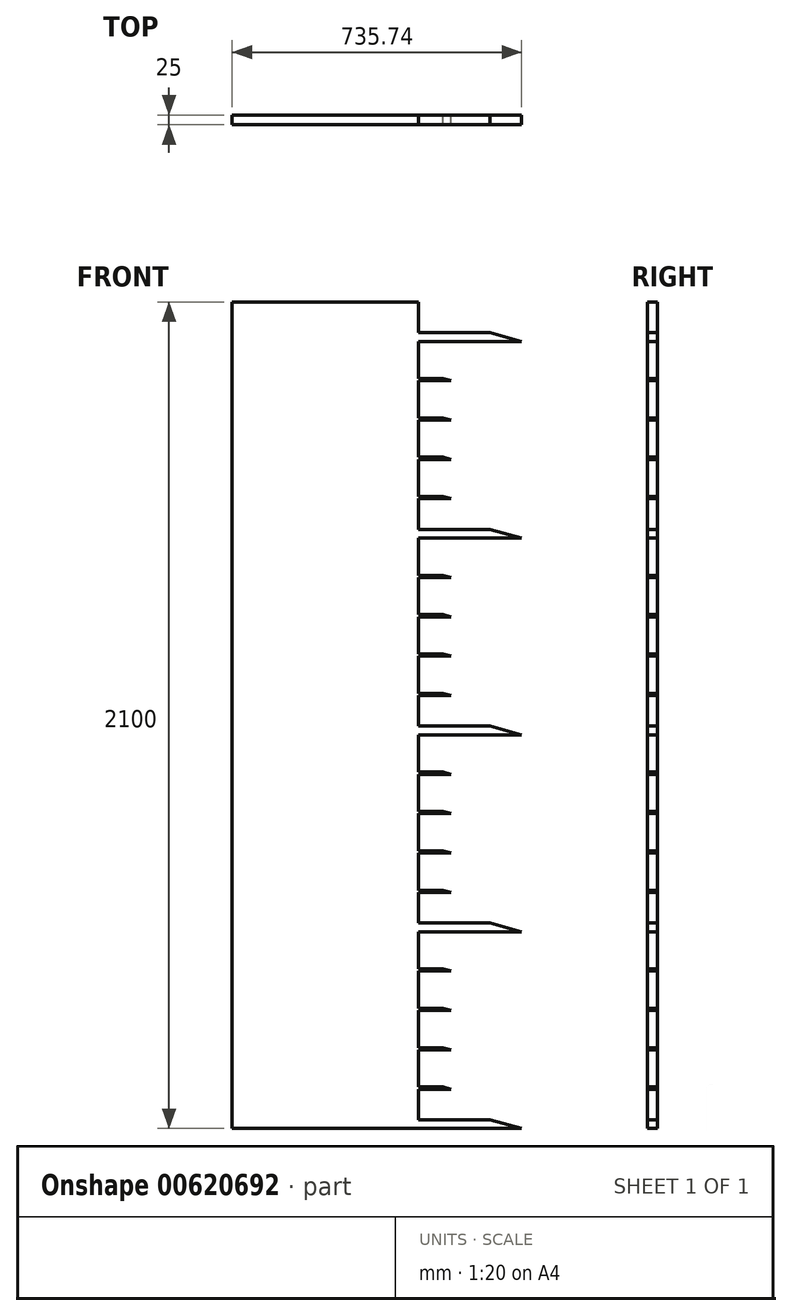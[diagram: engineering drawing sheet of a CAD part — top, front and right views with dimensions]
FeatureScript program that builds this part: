
annotation { "Feature Type Name" : "Feature", "Feature Type Description" : "" }
export const myFeature = defineFeature(function(context is Context, id is Id, definition is map)
    precondition{}
    {
        {
            var Q0;
            Q0=qCreatedBy(makeId("Front.planeOp"),FACE);
            var sketch = newSketch(context, id + "F0", { "sketchPlane" : qUnion([Q0])});
            skLineSegment(sketch, "E0.bottom", {"start": v(0, 0) * mm, "end": v(474.15, 0) * mm});
            skLineSegment(sketch, "E0.top", {"start": v(0, 2100) * mm, "end": v(474.15, 2100) * mm});
            skLineSegment(sketch, "E0.left", {"start": v(0, 0) * mm, "end": v(0, 2100) * mm});
            skLineSegment(sketch, "E0.right", {"start": v(474.15, 0) * mm, "end": v(474.15, 2100) * mm});
            skLineSegment(sketch, "E1.bottom", {"start": v(474.15, 0) * mm, "end": v(735.74, 0) * mm});
            skLineSegment(sketch, "E1.top", {"start": v(474.15, 22.4) * mm, "end": v(655.59, 22.4) * mm});
            skLineSegment(sketch, "E1.left", {"start": v(474.15, 0) * mm, "end": v(474.15, 22.4) * mm});
            skLineSegment(sketch, "E1.right", {"start": v(735.74, 0) * mm, "end": v(655.59, 22.4) * mm});
            skLineSegment(sketch, "E2.0.1.0", {"start": v(735.74, 500) * mm, "end": v(655.59, 522.4) * mm});
            skLineSegment(sketch, "E2.0.1.1", {"start": v(474.15, 500) * mm, "end": v(474.15, 522.4) * mm});
            skLineSegment(sketch, "E2.0.1.2", {"start": v(474.15, 522.4) * mm, "end": v(655.59, 522.4) * mm});
            skLineSegment(sketch, "E2.0.1.3", {"start": v(474.15, 500) * mm, "end": v(735.74, 500) * mm});
            skLineSegment(sketch, "E2.0.2.0", {"start": v(735.74, 1000) * mm, "end": v(655.59, 1022.4) * mm});
            skLineSegment(sketch, "E2.0.2.1", {"start": v(474.15, 1000) * mm, "end": v(474.15, 1022.4) * mm});
            skLineSegment(sketch, "E2.0.2.2", {"start": v(474.15, 1022.4) * mm, "end": v(655.59, 1022.4) * mm});
            skLineSegment(sketch, "E2.0.2.3", {"start": v(474.15, 1000) * mm, "end": v(735.74, 1000) * mm});
            skLineSegment(sketch, "E2.direction1", {"start": v(474.15, 0) * mm, "end": v(499.15, 0) * mm, "construction": true});
            skLineSegment(sketch, "E2.direction2", {"start": v(474.15, 0) * mm, "end": v(474.15, 500) * mm, "construction": true});
            skLineSegment(sketch, "E3.0.0.3", {"start": v(735.74, 1500) * mm, "end": v(655.59, 1522.4) * mm});
            skLineSegment(sketch, "E3.3.0.3", {"start": v(474.15, 1500) * mm, "end": v(474.15, 1522.4) * mm});
            skLineSegment(sketch, "E3.6.0.3", {"start": v(474.15, 1522.4) * mm, "end": v(655.59, 1522.4) * mm});
            skLineSegment(sketch, "E3.9.0.3", {"start": v(474.15, 1500) * mm, "end": v(735.74, 1500) * mm});
            skLineSegment(sketch, "E3.0.0.4", {"start": v(735.74, 2000) * mm, "end": v(655.59, 2022.4) * mm});
            skLineSegment(sketch, "E3.3.0.4", {"start": v(474.15, 2000) * mm, "end": v(474.15, 2022.4) * mm});
            skLineSegment(sketch, "E3.6.0.4", {"start": v(474.15, 2022.4) * mm, "end": v(655.59, 2022.4) * mm});
            skLineSegment(sketch, "E3.9.0.4", {"start": v(474.15, 2000) * mm, "end": v(735.74, 2000) * mm});
            skLineSegment(sketch, "E4.bottom", {"start": v(474.15, 0) * mm, "end": v(556.55, 0) * mm});
            skLineSegment(sketch, "E4.top", {"start": v(474.15, 5.45) * mm, "end": v(535.71, 5.45) * mm});
            skLineSegment(sketch, "E4.left", {"start": v(474.15, 0) * mm, "end": v(474.15, 5.45) * mm});
            skLineSegment(sketch, "E4.right", {"start": v(556.55, 0) * mm, "end": v(535.71, 5.45) * mm});
            skLineSegment(sketch, "E5.0.1.0", {"start": v(474.15, 105.45) * mm, "end": v(535.71, 105.45) * mm});
            skLineSegment(sketch, "E5.0.1.1", {"start": v(556.55, 100) * mm, "end": v(535.71, 105.45) * mm});
            skLineSegment(sketch, "E5.0.1.2", {"start": v(474.15, 100) * mm, "end": v(556.55, 100) * mm});
            skLineSegment(sketch, "E5.0.2.0", {"start": v(474.15, 205.45) * mm, "end": v(535.71, 205.45) * mm});
            skLineSegment(sketch, "E5.0.2.1", {"start": v(556.55, 200) * mm, "end": v(535.71, 205.45) * mm});
            skLineSegment(sketch, "E5.0.2.2", {"start": v(474.15, 200) * mm, "end": v(556.55, 200) * mm});
            skLineSegment(sketch, "E5.0.3.0", {"start": v(474.15, 305.45) * mm, "end": v(535.71, 305.45) * mm});
            skLineSegment(sketch, "E5.0.3.1", {"start": v(556.55, 300) * mm, "end": v(535.71, 305.45) * mm});
            skLineSegment(sketch, "E5.0.3.2", {"start": v(474.15, 300) * mm, "end": v(556.55, 300) * mm});
            skLineSegment(sketch, "E5.0.4.0", {"start": v(474.15, 405.45) * mm, "end": v(535.71, 405.45) * mm});
            skLineSegment(sketch, "E5.0.4.1", {"start": v(556.55, 400) * mm, "end": v(535.71, 405.45) * mm});
            skLineSegment(sketch, "E5.0.4.2", {"start": v(474.15, 400) * mm, "end": v(556.55, 400) * mm});
            skLineSegment(sketch, "E5.0.5.0", {"start": v(474.15, 505.45) * mm, "end": v(535.71, 505.45) * mm});
            skLineSegment(sketch, "E5.0.5.1", {"start": v(556.55, 500) * mm, "end": v(535.71, 505.45) * mm});
            skLineSegment(sketch, "E5.0.5.2", {"start": v(474.15, 500) * mm, "end": v(556.55, 500) * mm});
            skLineSegment(sketch, "E5.0.6.0", {"start": v(474.15, 605.45) * mm, "end": v(535.71, 605.45) * mm});
            skLineSegment(sketch, "E5.0.6.1", {"start": v(556.55, 600) * mm, "end": v(535.71, 605.45) * mm});
            skLineSegment(sketch, "E5.0.6.2", {"start": v(474.15, 600) * mm, "end": v(556.55, 600) * mm});
            skLineSegment(sketch, "E5.0.7.0", {"start": v(474.15, 705.45) * mm, "end": v(535.71, 705.45) * mm});
            skLineSegment(sketch, "E5.0.7.1", {"start": v(556.55, 700) * mm, "end": v(535.71, 705.45) * mm});
            skLineSegment(sketch, "E5.0.7.2", {"start": v(474.15, 700) * mm, "end": v(556.55, 700) * mm});
            skLineSegment(sketch, "E5.0.8.0", {"start": v(474.15, 805.45) * mm, "end": v(535.71, 805.45) * mm});
            skLineSegment(sketch, "E5.0.8.1", {"start": v(556.55, 800) * mm, "end": v(535.71, 805.45) * mm});
            skLineSegment(sketch, "E5.0.8.2", {"start": v(474.15, 800) * mm, "end": v(556.55, 800) * mm});
            skLineSegment(sketch, "E5.0.9.0", {"start": v(474.15, 905.45) * mm, "end": v(535.71, 905.45) * mm});
            skLineSegment(sketch, "E5.0.9.1", {"start": v(556.55, 900) * mm, "end": v(535.71, 905.45) * mm});
            skLineSegment(sketch, "E5.0.9.2", {"start": v(474.15, 900) * mm, "end": v(556.55, 900) * mm});
            skLineSegment(sketch, "E5.0.10.0", {"start": v(474.15, 1005.45) * mm, "end": v(535.71, 1005.45) * mm});
            skLineSegment(sketch, "E5.0.10.1", {"start": v(556.55, 1000) * mm, "end": v(535.71, 1005.45) * mm});
            skLineSegment(sketch, "E5.0.10.2", {"start": v(474.15, 1000) * mm, "end": v(556.55, 1000) * mm});
            skLineSegment(sketch, "E5.0.11.0", {"start": v(474.15, 1105.45) * mm, "end": v(535.71, 1105.45) * mm});
            skLineSegment(sketch, "E5.0.11.1", {"start": v(556.55, 1100) * mm, "end": v(535.71, 1105.45) * mm});
            skLineSegment(sketch, "E5.0.11.2", {"start": v(474.15, 1100) * mm, "end": v(556.55, 1100) * mm});
            skLineSegment(sketch, "E5.0.12.0", {"start": v(474.15, 1205.45) * mm, "end": v(535.71, 1205.45) * mm});
            skLineSegment(sketch, "E5.0.12.1", {"start": v(556.55, 1200) * mm, "end": v(535.71, 1205.45) * mm});
            skLineSegment(sketch, "E5.0.12.2", {"start": v(474.15, 1200) * mm, "end": v(556.55, 1200) * mm});
            skLineSegment(sketch, "E5.0.13.0", {"start": v(474.15, 1305.45) * mm, "end": v(535.71, 1305.45) * mm});
            skLineSegment(sketch, "E5.0.13.1", {"start": v(556.55, 1300) * mm, "end": v(535.71, 1305.45) * mm});
            skLineSegment(sketch, "E5.0.13.2", {"start": v(474.15, 1300) * mm, "end": v(556.55, 1300) * mm});
            skLineSegment(sketch, "E5.0.14.0", {"start": v(474.15, 1405.45) * mm, "end": v(535.71, 1405.45) * mm});
            skLineSegment(sketch, "E5.0.14.1", {"start": v(556.55, 1400) * mm, "end": v(535.71, 1405.45) * mm});
            skLineSegment(sketch, "E5.0.14.2", {"start": v(474.15, 1400) * mm, "end": v(556.55, 1400) * mm});
            skLineSegment(sketch, "E5.0.15.0", {"start": v(474.15, 1505.45) * mm, "end": v(535.71, 1505.45) * mm});
            skLineSegment(sketch, "E5.0.15.1", {"start": v(556.55, 1500) * mm, "end": v(535.71, 1505.45) * mm});
            skLineSegment(sketch, "E5.0.15.2", {"start": v(474.15, 1500) * mm, "end": v(556.55, 1500) * mm});
            skLineSegment(sketch, "E5.0.16.0", {"start": v(474.15, 1605.45) * mm, "end": v(535.71, 1605.45) * mm});
            skLineSegment(sketch, "E5.0.16.1", {"start": v(556.55, 1600) * mm, "end": v(535.71, 1605.45) * mm});
            skLineSegment(sketch, "E5.0.16.2", {"start": v(474.15, 1600) * mm, "end": v(556.55, 1600) * mm});
            skLineSegment(sketch, "E5.0.17.0", {"start": v(474.15, 1705.45) * mm, "end": v(535.71, 1705.45) * mm});
            skLineSegment(sketch, "E5.0.17.1", {"start": v(556.55, 1700) * mm, "end": v(535.71, 1705.45) * mm});
            skLineSegment(sketch, "E5.0.17.2", {"start": v(474.15, 1700) * mm, "end": v(556.55, 1700) * mm});
            skLineSegment(sketch, "E5.0.18.0", {"start": v(474.15, 1805.45) * mm, "end": v(535.71, 1805.45) * mm});
            skLineSegment(sketch, "E5.0.18.1", {"start": v(556.55, 1800) * mm, "end": v(535.71, 1805.45) * mm});
            skLineSegment(sketch, "E5.0.18.2", {"start": v(474.15, 1800) * mm, "end": v(556.55, 1800) * mm});
            skLineSegment(sketch, "E5.0.19.0", {"start": v(474.15, 1905.45) * mm, "end": v(535.71, 1905.45) * mm});
            skLineSegment(sketch, "E5.0.19.1", {"start": v(556.55, 1900) * mm, "end": v(535.71, 1905.45) * mm});
            skLineSegment(sketch, "E5.0.19.2", {"start": v(474.15, 1900) * mm, "end": v(556.55, 1900) * mm});
            skLineSegment(sketch, "E5.direction2", {"start": v(474.15, 0) * mm, "end": v(474.15, 100) * mm, "construction": true});
            skSolve(sketch);
        }
        {
            var Q0;
            Q0=qSketchRegion(id+"F0",true);
            extrude(context, id + "F1", {"entities" : qUnion([Q0]), "depth" : 25 * mm, "offsetDistance" : 25 * mm});
        }
    });
